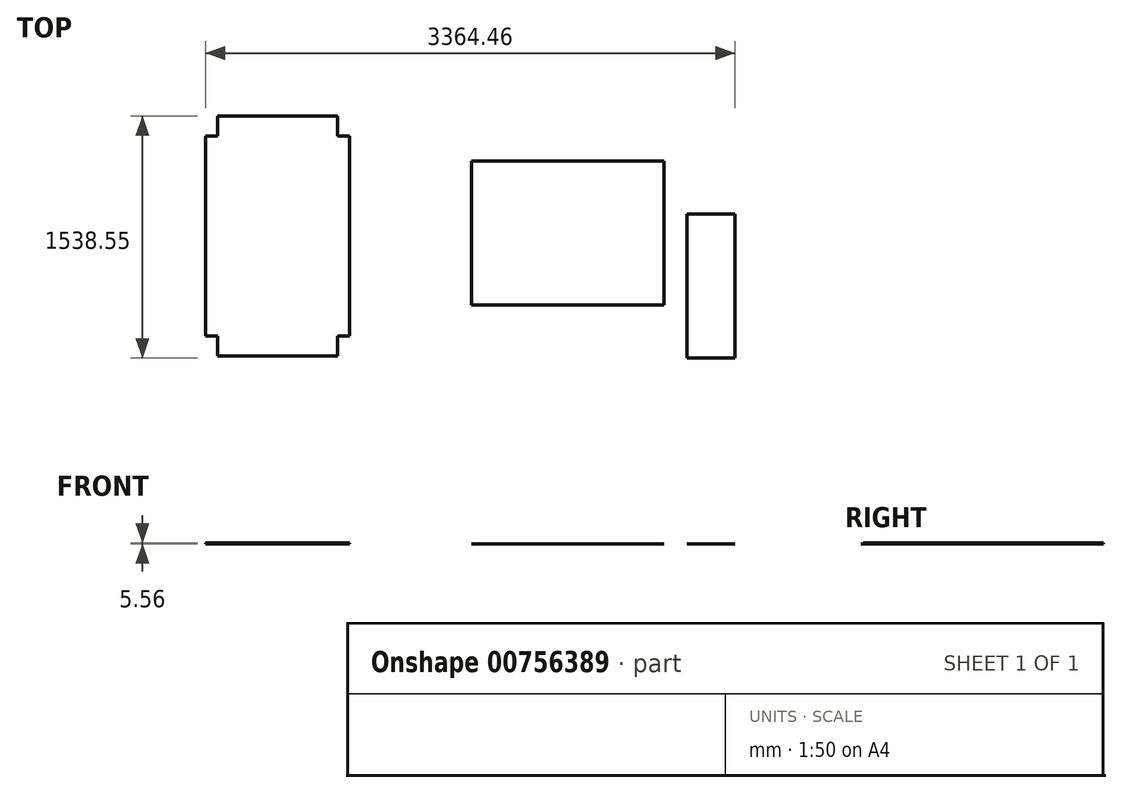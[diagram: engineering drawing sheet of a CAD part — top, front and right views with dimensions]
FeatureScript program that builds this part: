
annotation { "Feature Type Name" : "Feature", "Feature Type Description" : "" }
export const myFeature = defineFeature(function(context is Context, id is Id, definition is map)
    precondition{}
    {
        {
            var Q0;
            Q0=qCreatedBy(makeId("Top.planeOp"),FACE);
            var sketch = newSketch(context, id + "F0", { "sketchPlane" : qUnion([Q0])});
            skLineSegment(sketch, "E0.bottom", {"start": v(0, 2438.4) * mm, "end": v(1219.2, 2438.4) * mm});
            skLineSegment(sketch, "E0.top", {"start": v(0, 0) * mm, "end": v(1219.2, 0) * mm});
            skLineSegment(sketch, "E1", {"start": v(0, 1524) * mm, "end": v(914.4, 1524) * mm});
            skLineSegment(sketch, "E2", {"start": v(914.4, 1524) * mm, "end": v(914.4, 0) * mm});
            skLineSegment(sketch, "E3", {"start": v(914.4, 1524) * mm, "end": v(1219.2, 1524) * mm});
            skLineSegment(sketch, "E4", {"start": v(914.4, 914.4) * mm, "end": v(1219.2, 914.4) * mm});
            skLineSegment(sketch, "E5", {"start": v(0, 2438.4) * mm, "end": v(0, 0) * mm});
            skLineSegment(sketch, "E6", {"start": v(1219.2, 0) * mm, "end": v(1219.2, 2438.4) * mm});
            skLineSegment(sketch, "E7.bottom", {"start": v(3031.42, 739.7) * mm, "end": v(3945.82, 739.7) * mm});
            skLineSegment(sketch, "E7.top", {"start": v(3031.42, 2263.7) * mm, "end": v(3945.82, 2263.7) * mm});
            skLineSegment(sketch, "E7.left", {"start": v(3031.42, 739.7) * mm, "end": v(3031.42, 2263.7) * mm});
            skLineSegment(sketch, "E7.right", {"start": v(3945.82, 739.7) * mm, "end": v(3945.82, 2263.7) * mm});
            skLineSegment(sketch, "E8.bottom", {"start": v(4723.4, 1063.9) * mm, "end": v(5942.6, 1063.9) * mm});
            skLineSegment(sketch, "E8.top", {"start": v(4723.4, 1978.3) * mm, "end": v(5942.6, 1978.3) * mm});
            skLineSegment(sketch, "E8.left", {"start": v(4723.4, 1063.9) * mm, "end": v(4723.4, 1978.3) * mm});
            skLineSegment(sketch, "E8.right", {"start": v(5942.6, 1063.9) * mm, "end": v(5942.6, 1978.3) * mm});
            skLineSegment(sketch, "E9.bottom", {"start": v(6091.08, 725.15) * mm, "end": v(6395.88, 725.15) * mm});
            skLineSegment(sketch, "E9.top", {"start": v(6091.08, 1639.55) * mm, "end": v(6395.88, 1639.55) * mm});
            skLineSegment(sketch, "E9.left", {"start": v(6091.08, 725.15) * mm, "end": v(6091.08, 1639.55) * mm});
            skLineSegment(sketch, "E9.right", {"start": v(6395.88, 725.15) * mm, "end": v(6395.88, 1639.55) * mm});
            skLineSegment(sketch, "E10", {"start": v(3488.62, 2263.7) * mm, "end": v(3488.62, 739.7) * mm, "construction": true});
            skLineSegment(sketch, "E11", {"start": v(3031.42, 1501.7) * mm, "end": v(3945.82, 1501.7) * mm, "construction": true});
            skLineSegment(sketch, "E12", {"start": v(3107.62, 2263.7) * mm, "end": v(3107.62, 2136.7) * mm});
            skLineSegment(sketch, "E13", {"start": v(3107.62, 2136.7) * mm, "end": v(3031.42, 2136.7) * mm});
            skLineSegment(sketch, "E14.MirrorCS", {"start": v(3869.62, 2136.7) * mm, "end": v(3945.82, 2136.7) * mm});
            skLineSegment(sketch, "E15.MirrorCS", {"start": v(3869.62, 2263.7) * mm, "end": v(3869.62, 2136.7) * mm});
            skLineSegment(sketch, "E16.MirrorCS", {"start": v(3107.62, 866.7) * mm, "end": v(3031.42, 866.7) * mm});
            skLineSegment(sketch, "E17.MirrorCS", {"start": v(3107.62, 739.7) * mm, "end": v(3107.62, 866.7) * mm});
            skLineSegment(sketch, "E18.MirrorCS", {"start": v(3869.62, 739.7) * mm, "end": v(3869.62, 866.7) * mm});
            skLineSegment(sketch, "E19.MirrorCS", {"start": v(3869.62, 866.7) * mm, "end": v(3945.82, 866.7) * mm});
            skSolve(sketch);
        }
        {
            var Q0;
            {var subQ5=sQuery(id+"F0.wireOp",EDGE,"E12");Q0=makeQuery(id+"F0.imprint","IMPRINT",FACE,{"disambiguationData":[TD([[makeQuery(id+"F0.imprint","IMPRINT",EDGE,{"derivedFrom":subQ5}),1.0]])]});}
            extrude(context, id + "F1", {"entities" : qUnion([Q0]), "depth" : 5.56 * mm, "offsetDistance" : 30.48 * mm});
        }
        {
            var Q0;
            Q0=makeQuery(id+"F0.imprint","IMPRINT",FACE,{"disambiguationData":[TD([[makeQuery(id+"F0.imprint","IMPRINT",EDGE,{"derivedFrom":sQuery(id+"F0.wireOp",EDGE,"E8.bottom")}),1.0]])]});
            extrude(context, id + "F2", {"entities" : qUnion([Q0]), "depth" : 7 / 812.8 * mm, "offsetDistance" : 30.48 * mm});
        }
        {
            var Q0;
            Q0=makeQuery(id+"F0.imprint","IMPRINT",FACE,{"disambiguationData":[TD([[makeQuery(id+"F0.imprint","IMPRINT",EDGE,{"derivedFrom":sQuery(id+"F0.wireOp",EDGE,"E9.bottom")}),1.0]])]});
            extrude(context, id + "F3", {"entities" : qUnion([Q0]), "depth" : 7 / 812.8 * mm, "offsetDistance" : 30.48 * mm});
        }
    });
